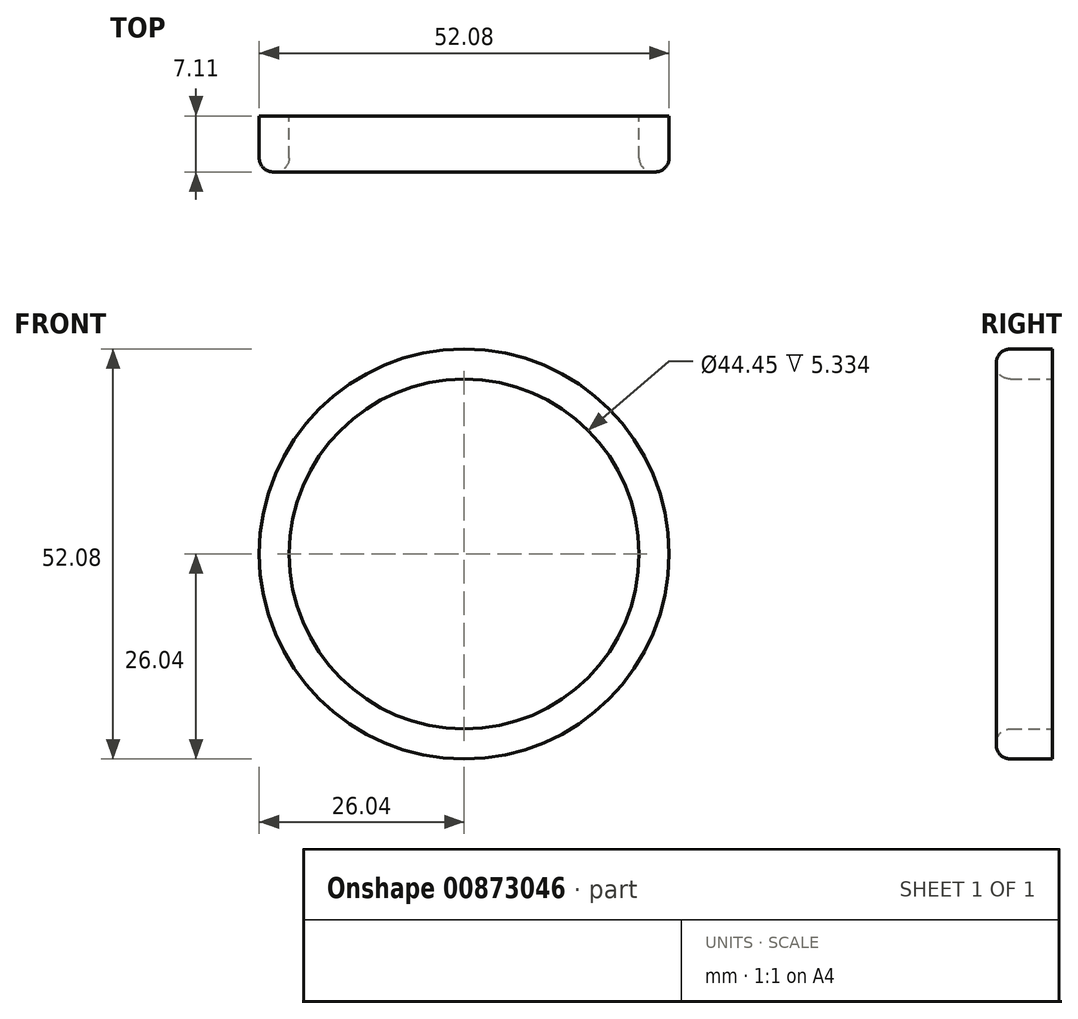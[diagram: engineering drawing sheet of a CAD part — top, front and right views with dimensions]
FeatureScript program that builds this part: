
annotation { "Feature Type Name" : "Feature", "Feature Type Description" : "" }
export const myFeature = defineFeature(function(context is Context, id is Id, definition is map)
    precondition{}
    {
        {
            var Q0;
            Q0=qCreatedBy(makeId("Front.planeOp"),FACE);
            var sketch = newSketch(context, id + "F0", { "sketchPlane" : qUnion([Q0])});
            skCircle(sketch, "E0", {"center": v(0, 0) * mm, "radius": 26.04 * mm});
            skCircle(sketch, "E1", {"center": v(0, 0) * mm, "radius": 22.23 * mm});
            skSolve(sketch);
        }
        {
            var Q0;
            Q0=makeQuery(id+"F0.imprint","IMPRINT",FACE,{"disambiguationData":[TD([[makeQuery(id+"F0.imprint","IMPRINT",EDGE,{"derivedFrom":sQuery(id+"F0.wireOp",EDGE,"E0")}),1.0]])]});
            extrude(context, id + "F1", {"entities" : qUnion([Q0]), "depth" : 7.11 * mm, "offsetDistance" : 25.4 * mm});
        }
        {
            var Q0;
            Q0=makeQuery(id+"F1.opExtrude","CAP_EDGE",EDGE,{"disambiguationData":[OSD([sQuery(id+"F0.wireOp",EDGE,"E0")])],"isStart":false});
            var Q1;
            Q1=makeQuery(id+"F1.opExtrude","CAP_EDGE",EDGE,{"disambiguationData":[OSD([sQuery(id+"F0.wireOp",EDGE,"E1")])],"isStart":false});
            fillet(context, id + "F2", {"entities" : qUnion([Q0, Q1]), "radius" : 1.78 * mm, "width" : 5.08 * mm, "tangentPropagation" : true, "blendControlType" : BlendControlType.RADIUS, "defaultsChanged" : false, "isAsymmetric" : false, "otherRadius" : 5.08 * mm, "flipAsymmetric" : false, "isPartial" : false, "partialFirstEdgeTotalParameter" : 0.01, "partialOppositeParameter" : true, "secondBound" : false, "partialSecondEdgeTotalParameter" : 0.99, "vertexSettings" : [], "pointOnEdgeSettings" : [], "allowEdgeOverflow" : false, "smoothCorners" : false, "filletType" : FilletType.EDGE});
        }
    });
